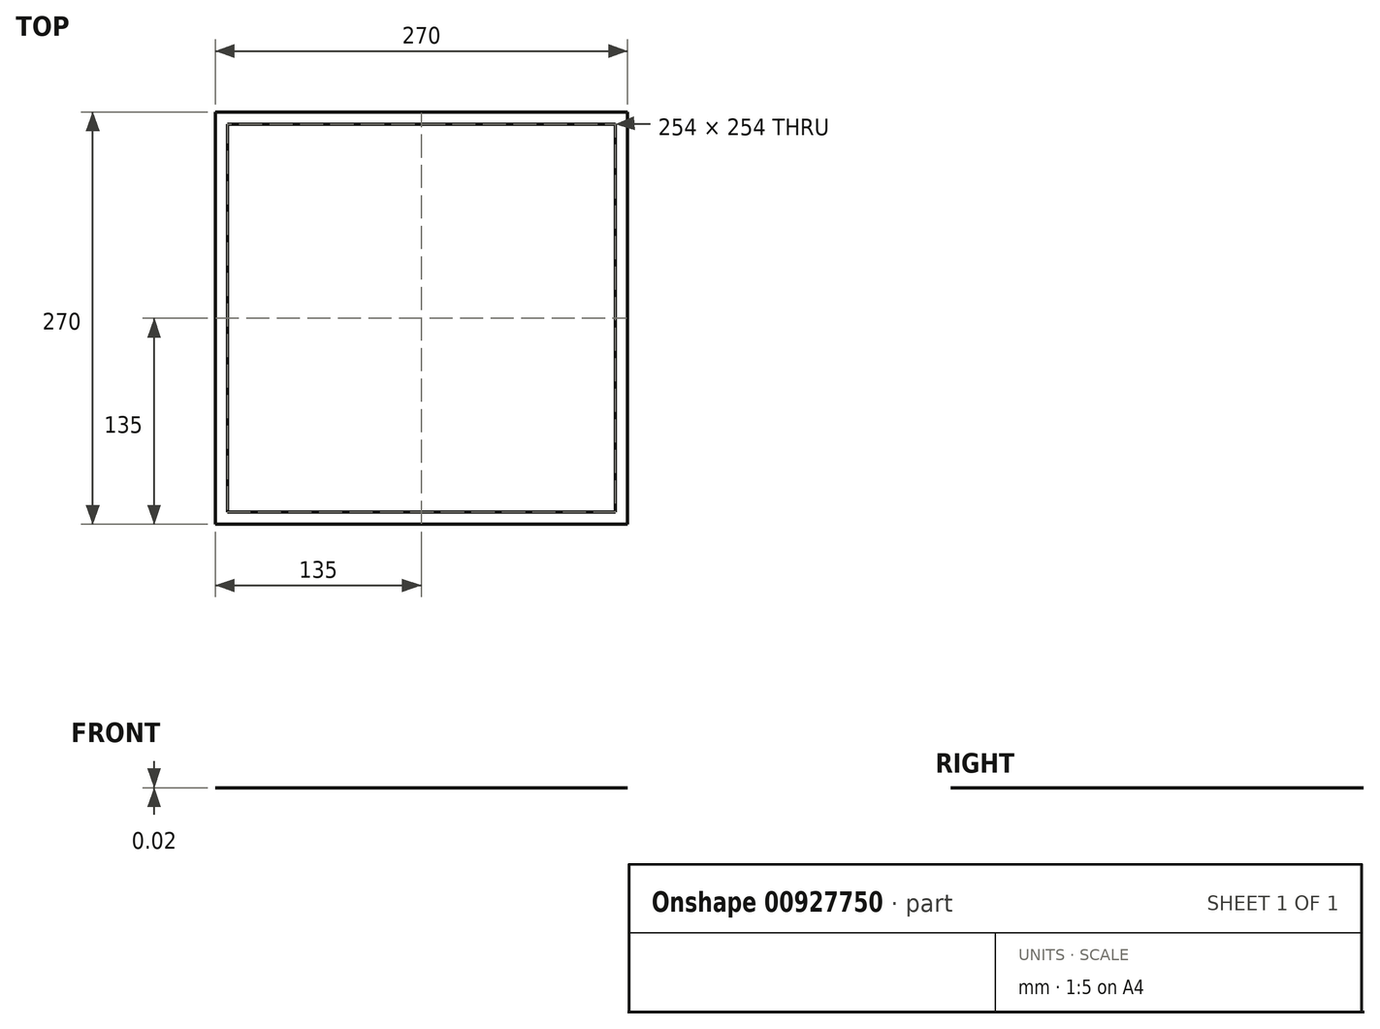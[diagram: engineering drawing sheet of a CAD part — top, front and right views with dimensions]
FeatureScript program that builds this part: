
annotation { "Feature Type Name" : "Feature", "Feature Type Description" : "" }
export const myFeature = defineFeature(function(context is Context, id is Id, definition is map)
    precondition{}
    {
        {
            var Q0;
            Q0=qCreatedBy(makeId("Top.planeOp"),FACE);
            var sketch = newSketch(context, id + "F0", { "sketchPlane" : qUnion([Q0])});
            skLineSegment(sketch, "E0.bottom", {"start": v(127, 127) * mm, "end": v(-127, 127) * mm});
            skLineSegment(sketch, "E0.top", {"start": v(127, -127) * mm, "end": v(-127, -127) * mm});
            skLineSegment(sketch, "E0.left", {"start": v(127, 127) * mm, "end": v(127, -127) * mm});
            skLineSegment(sketch, "E0.right", {"start": v(-127, 127) * mm, "end": v(-127, -127) * mm});
            skPoint(sketch, "E0.middle", {"position": v(0, 0) * mm});
            skLineSegment(sketch, "E1.bottom", {"start": v(135, 135) * mm, "end": v(-135, 135) * mm});
            skLineSegment(sketch, "E1.top", {"start": v(135, -135) * mm, "end": v(-135, -135) * mm});
            skLineSegment(sketch, "E1.left", {"start": v(135, 135) * mm, "end": v(135, -135) * mm});
            skLineSegment(sketch, "E1.right", {"start": v(-135, 135) * mm, "end": v(-135, -135) * mm});
            skSolve(sketch);
        }
        {
            var Q0;
            Q0=makeQuery(id+"F0.imprint","IMPRINT",FACE,{"disambiguationData":[TD([[makeQuery(id+"F0.imprint","IMPRINT",EDGE,{"derivedFrom":sQuery(id+"F0.wireOp",EDGE,"E0.bottom")}),-1.0]])]});
            extrude(context, id + "F1", {"entities" : qUnion([Q0]), "depth" : 10 / 406.4 * mm, "offsetDistance" : 25.4 * mm});
        }
    });
